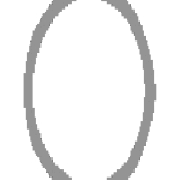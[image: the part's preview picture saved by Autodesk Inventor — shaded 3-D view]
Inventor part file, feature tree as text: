
AUTODESK INVENTOR PART (.ipt)
format: ipt  version: 2021 (Build 250183000, 183)  size: 160,768 bytes
history: native  units: in
note: dims shown in document units (in); Inventor stores cm internally (conversion verified against a paired STEP export)
features: other x5, sketch x2, sweep x1, plane x1
ambient origin geometry x8: Origin, YZ Plane, XZ Plane, XY Plane, X Axis, Y Axis, Z Axis, Center Point
bodies: Solid1 (feature_tree), Body (feature_tree)
feature tree (9):
  other  "Driven Length"
  other  "Frame Generator"
  other  "Start Plane"
  other  "End Plane"
  sweep  "Sweep Path"
  other  "Orientation Work Plane"
  sketch  "Sketch2"  dims[d0=1.0in d1=0.065in]
  plane  "Work Plane3"
  sketch  "Sketch3"  dims[d2=7.854in d4=-0.0in d5=7.854in d8=90.0deg d9=7.854in d10=0.0in d11=0.0in]
